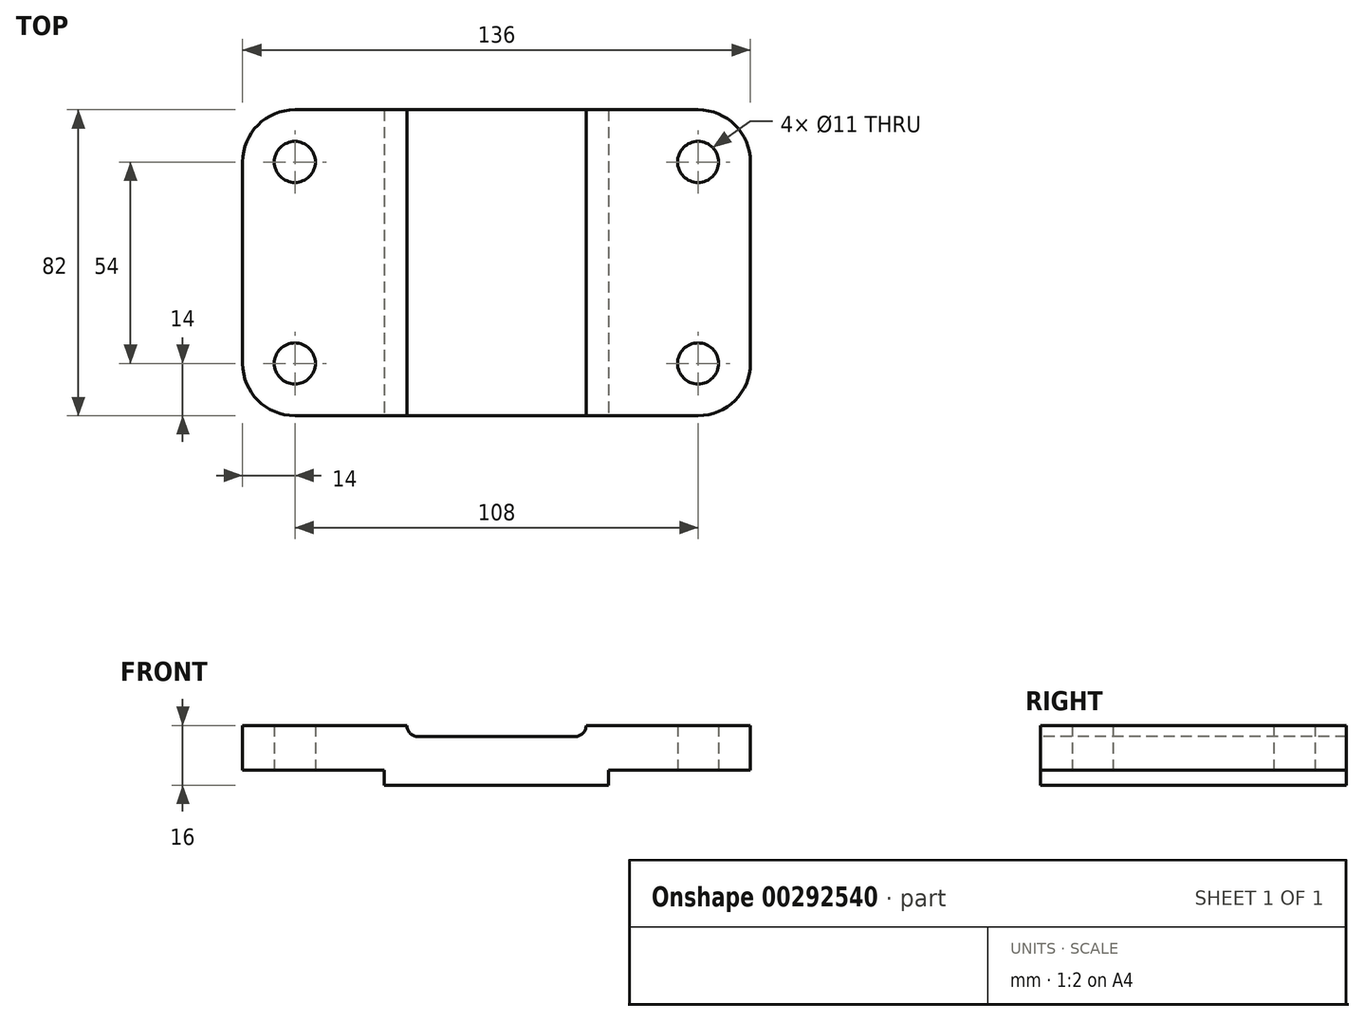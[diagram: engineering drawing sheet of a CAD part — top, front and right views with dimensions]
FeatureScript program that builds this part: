
annotation { "Feature Type Name" : "Feature", "Feature Type Description" : "" }
export const myFeature = defineFeature(function(context is Context, id is Id, definition is map)
    precondition{}
    {
        {
            var Q0;
            Q0=qCreatedBy(makeId("Top.planeOp"),FACE);
            var sketch = newSketch(context, id + "F0", { "sketchPlane" : qUnion([Q0])});
            skLineSegment(sketch, "E0.bottom", {"start": v(14, 0) * mm, "end": v(122, 0) * mm});
            skLineSegment(sketch, "E0.top", {"start": v(14, 82) * mm, "end": v(122, 82) * mm});
            skLineSegment(sketch, "E0.left", {"start": v(0, 14) * mm, "end": v(0, 68) * mm});
            skLineSegment(sketch, "E0.right", {"start": v(136, 14) * mm, "end": v(136, 68) * mm});
            skPoint(sketch, "E1.visualSharp", {"position": v(0, 82) * mm});
            skArc(sketch, "E1.filletArc", {"start": v(14, 82) * mm, "mid": v(4.1, 77.9) * mm, "end": v(0, 68) * mm});
            skPoint(sketch, "E2.visualSharp", {"position": v(0, 0) * mm});
            skArc(sketch, "E2.filletArc", {"start": v(0, 14) * mm, "mid": v(4.1, 4.1) * mm, "end": v(14, 0) * mm});
            skPoint(sketch, "E3.visualSharp", {"position": v(136, 82) * mm});
            skArc(sketch, "E3.filletArc", {"start": v(136, 68) * mm, "mid": v(131.9, 77.9) * mm, "end": v(122, 82) * mm});
            skPoint(sketch, "E4.visualSharp", {"position": v(136, 0) * mm});
            skArc(sketch, "E4.filletArc", {"start": v(122, 0) * mm, "mid": v(131.9, 4.1) * mm, "end": v(136, 14) * mm});
            skCircle(sketch, "E5", {"center": v(14, 68) * mm, "radius": 5.5 * mm});
            skCircle(sketch, "E6", {"center": v(14, 14) * mm, "radius": 5.5 * mm});
            skCircle(sketch, "E7", {"center": v(122, 68) * mm, "radius": 5.5 * mm});
            skCircle(sketch, "E8", {"center": v(122, 14) * mm, "radius": 5.5 * mm});
            skSolve(sketch);
        }
        {
            var Q0;
            Q0 = qSketchRegion(id + "F0", true);
            extrude(context, id + "F1", {"entities" : qUnion([Q0]), "depth" : 16 * mm});
        }
        {
            var Q0;
            Q0=makeQuery(id+"F1.opExtrude","SWEPT_FACE",FACE,{"disambiguationData":[OSD([sQuery(id+"F0.wireOp",EDGE,"E0.bottom")])]});
            var sketch = newSketch(context, id + "F2", { "sketchPlane" : qUnion([Q0])});
            skLineSegment(sketch, "E9", {"start": v(0, 19.25) * mm, "end": v(44, 19.25) * mm, "construction": true});
            skLineSegment(sketch, "E10", {"start": v(0, -6.36) * mm, "end": v(38, -6.36) * mm, "construction": true});
            skArc(sketch, "E11", {"start": v(44, 16) * mm, "mid": v(44.88, 13.88) * mm, "end": v(47, 13) * mm});
            skLineSegment(sketch, "E12", {"start": v(136, -9.38) * mm, "end": v(136, 41.38) * mm, "construction": true});
            skLineSegment(sketch, "E13", {"start": v(136, -9.38) * mm, "end": v(98, -9.38) * mm, "construction": true});
            skLineSegment(sketch, "E14", {"start": v(136, 21.88) * mm, "end": v(92, 21.88) * mm, "construction": true});
            skArc(sketch, "E15", {"start": v(89, 13) * mm, "mid": v(91.12, 13.88) * mm, "end": v(92, 16) * mm});
            skLineSegment(sketch, "E16", {"start": v(47, 13) * mm, "end": v(89, 13) * mm});
            skLineSegment(sketch, "E17", {"start": v(38, 0) * mm, "end": v(38, 4) * mm});
            skLineSegment(sketch, "E18", {"start": v(38, 4) * mm, "end": v(0, 4) * mm});
            skLineSegment(sketch, "E19", {"start": v(0, 4) * mm, "end": v(0, 0) * mm});
            skLineSegment(sketch, "E20", {"start": v(0, 0) * mm, "end": v(38, 0) * mm});
            skLineSegment(sketch, "E21", {"start": v(136, 0) * mm, "end": v(98, 0) * mm});
            skLineSegment(sketch, "E22", {"start": v(98, 0) * mm, "end": v(98, 4) * mm});
            skLineSegment(sketch, "E23", {"start": v(98, 4) * mm, "end": v(136, 4) * mm});
            skLineSegment(sketch, "E24", {"start": v(136, 4) * mm, "end": v(136, 0) * mm});
            skSolve(sketch);
        }
        {
            var Q0;
            Q0 = qSketchRegion(id + "F2", true);
            var Q1;
            {var subQ0=sQuery(id+"F2.wireOp",EDGE,"E11");Q1=makeQuery(id+"F2.imprint","IMPRINT",FACE,{"disambiguationData":[TD([[makeQuery(id+"F2.imprint","IMPRINT",EDGE,{"derivedFrom":subQ0}),1.0]])]});}
            extrude(context, id + "F3", {"entities" : qUnion([Q0, Q1]), "operationType" : NewBodyOperationType.REMOVE, "endBound" : BoundingType.THROUGH_ALL, "oppositeDirection" : true, "depth" : 25 * mm});
        }
    });
